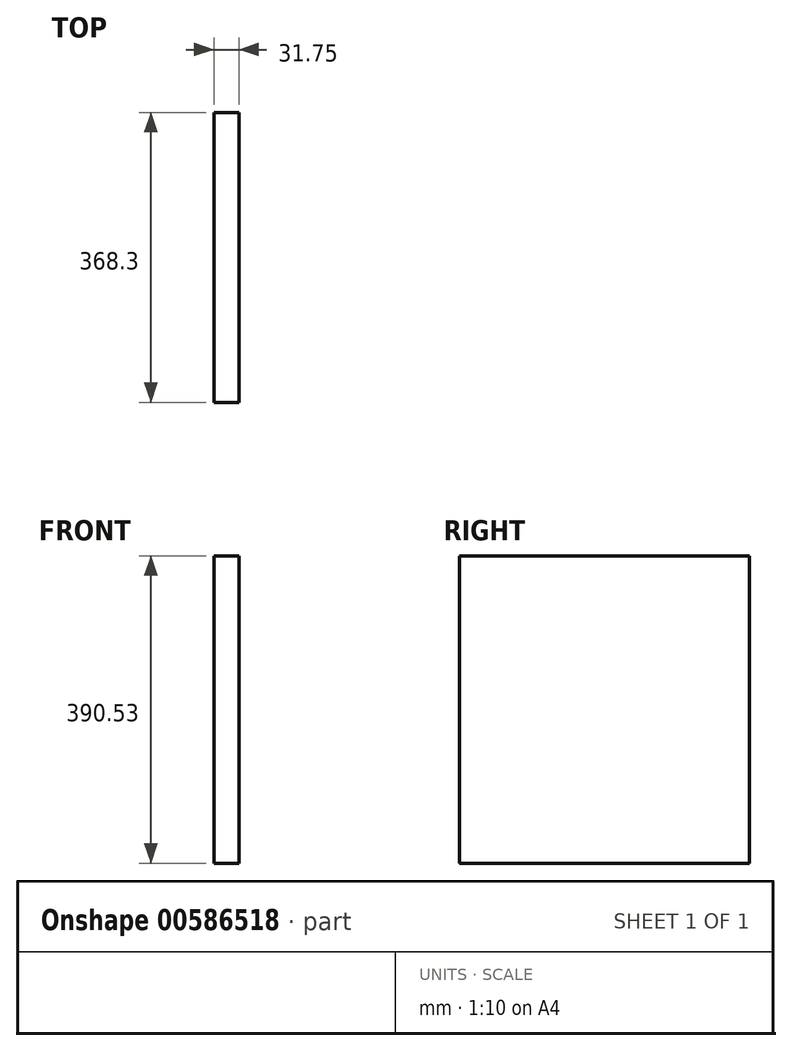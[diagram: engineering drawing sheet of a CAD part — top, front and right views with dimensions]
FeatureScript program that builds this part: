
annotation { "Feature Type Name" : "Feature", "Feature Type Description" : "" }
export const myFeature = defineFeature(function(context is Context, id is Id, definition is map)
    precondition{}
    {
        {
            var Q0;
            Q0=qCreatedBy(makeId("Front.planeOp"),FACE);
            var sketch = newSketch(context, id + "F0", { "sketchPlane" : qUnion([Q0])});
            skLineSegment(sketch, "E0.bottom", {"start": v(0, 0) * mm, "end": v(31.75, 0) * mm});
            skLineSegment(sketch, "E0.top", {"start": v(0, 390.53) * mm, "end": v(31.75, 390.53) * mm});
            skLineSegment(sketch, "E0.left", {"start": v(0, 0) * mm, "end": v(0, 390.53) * mm});
            skLineSegment(sketch, "E0.right", {"start": v(31.75, 0) * mm, "end": v(31.75, 390.53) * mm});
            skSolve(sketch);
        }
        {
            var Q0;
            Q0=makeQuery(id+"F0.imprint","IMPRINT",FACE,{"disambiguationData":[TD([[makeQuery(id+"F0.imprint","IMPRINT",EDGE,{"derivedFrom":sQuery(id+"F0.wireOp",EDGE,"E0.bottom")}),1.0]])]});
            extrude(context, id + "F1", {"entities" : qUnion([Q0]), "depth" : 368.3 * mm, "offsetDistance" : 25.4 * mm});
        }
    });
